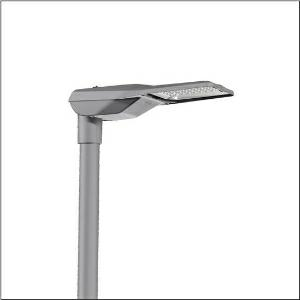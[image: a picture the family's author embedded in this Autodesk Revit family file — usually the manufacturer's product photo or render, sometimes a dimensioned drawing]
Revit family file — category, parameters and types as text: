
# Revit family: streetlight_sl_21_mini___pl52_5xe2h33s08gb_224a
name_source: partatom
category: Lighting Fixtures
units: mm (PartAtom-declared; Revit-internal decimal feet)

## family parameters
Cut with Voids When Loaded = No
Host = Face
Light Source = No
Part Type = Normal
Room Calculation Point = No
Round Connector Dimension = Use Diameter
Shared = No

## types (1)
- --- (1 x LED, 5840 lm, 40.4 W, 3000K)
    Apparent Load = 40 VA
    CIE Flux Codes = 27 59 98 100 100
    Color Rendering = 70
    Color Temperature = 3000K
    Default Elevation = 1800 mm
    Description = Streetlight SL 21 mini, mast luminaire, primary light control with lens, of PMMA, primary optical cover: cover, of toughened safety glass, transparent, light distribution: PL52, light emission: direct distribution, primary light characteristic: asymmetric, installation type: side-entry, post-top, LED, High Power LED, rated luminous flux: 5.840lm, luminous efficacy: 145lm/W, light colour: 730, colour temperature: 3000K, control gear: D4i, control: overheat protection, constant luminous flux control, time-dependent luminous flux control, flexible luminous flux parameterisation, pre-setting: logarithmic dimming characteristic, mains connection: 220..240V, AC, 50/60Hz, start of lifetime: 40W, end of service life: 41W, reduction: 19W, luminaire housing, of diecast aluminium, powder-coated, Siteco® metallic grey (DB 702S), corrosivity category C5 mid according to DIN EN ISO 12944, please order mast flange separately, inclination adjustable: 0°, 5°, 10°, 15°, sealing non-destructively replaceable, multi-level sealing system, length: 628mm, width: 235mm, height: 110mm, mast flange for spigot size: 42mm (side-entry): 5XC10008XM4, 60/48mm (side-entry/post-top): 5XC10108XM2, 76/60mm (side-entry/post-top): 5XC10108XM1, mounting height: 4..8m, Smart Interface above, protection rating (complete): IP66, insulation class (complete): insulation class II (safety insulation), certification: CE, ENEC, ENEC+, VDE, impact resistance: IK10, permissible operating ambient temperature for outdoor applications: -40..+50°C, standard-compliant lighting for roads and squares, packaging unit: 1 piece

Light Distribution: PL52
    Height = 110 mm
    Lamp = 1 x LED
    Lamp Light Flux = 5840 lm
    Lamp Power = 40.4 W
    Lamp count = 1
    Length = 625 mm
    Luminous efficacy = 145 lm/W
    Manufacturer = Siteco
    ModVariant = No
    Model = 5XE2H33S08GB
    Number of Poles = 1
    OnlyDefault = Yes
    Power Factor = 1
    Product Name = Streetlight SL 21 mini | PL52
    Product group = mast luminaire | pylon top
    ProductGroupID = 6100
    Protection Class = Protection class II
    Protection Degree = IP 66
    RLX_Detail_Level = 1
    RLX_Emergency_Light_Flux = 0 lm
    RLX_Emergency_Type = 0
    RLX_Emergency_Type_DB = No
    RlxData = <blob elided: 35809 chars, md5=e8e93826>
    Socket = socket
    Standby Power = 0 W
    System Light Flux = 5840 lm
    System Power = 40 W
    Type Comments = factory setting: luminous flux: 100 % | dim-lin: 254 | 812 mA
    Type Image = l_1003515.jpg
    URL = http://relux.com
    VarID = @adj_211505
    Voltage = 0 V
    Weight = 0.00 kg
    Width = 234 mm

## geometry (parser evidence)
native form markers: Blend x4, Sweep x11
no freeform markers — native parametric forms only
